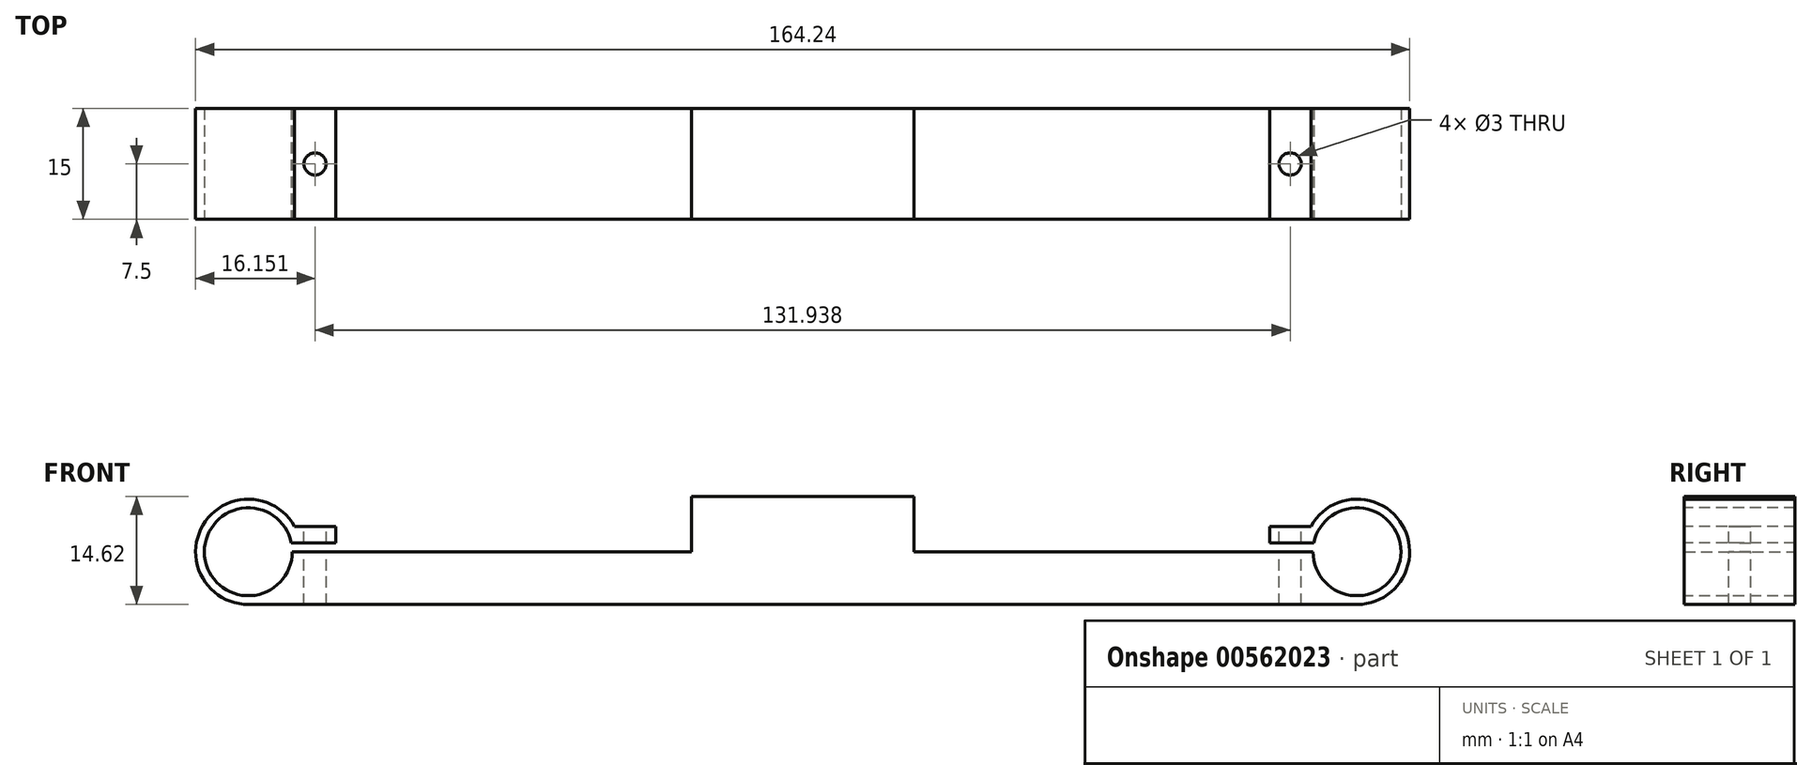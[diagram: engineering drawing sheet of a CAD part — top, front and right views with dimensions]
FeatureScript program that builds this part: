
annotation { "Feature Type Name" : "Feature", "Feature Type Description" : "" }
export const myFeature = defineFeature(function(context is Context, id is Id, definition is map)
    precondition{}
    {
        {
            var Q0;
            Q0=qCreatedBy(makeId("Front.planeOp"),FACE);
            var sketch = newSketch(context, id + "F0", { "sketchPlane" : qUnion([Q0])});
            skCircle(sketch, "E0", {"center": v(-75, 0) * mm, "radius": 5.95 * mm, "construction": true});
            skCircle(sketch, "E1", {"center": v(-75, 0) * mm, "radius": 7.12 * mm});
            skCircle(sketch, "E2", {"center": v(75, 0) * mm, "radius": 7.12 * mm});
            skLineSegment(sketch, "E3.bottom", {"start": v(-75, 0) * mm, "end": v(75.04, 0) * mm});
            skLineSegment(sketch, "E3.top", {"start": v(-75, -7.12) * mm, "end": v(75.04, -7.12) * mm});
            skLineSegment(sketch, "E3.left", {"start": v(-75, 0) * mm, "end": v(-75, -7.12) * mm});
            skLineSegment(sketch, "E3.right", {"start": v(75.04, 0) * mm, "end": v(75.04, -7.12) * mm});
            skSolve(sketch);
        }
        {
            var Q0;
            Q0=makeQuery(id+"F0.imprint","IMPRINT",FACE,{"disambiguationData":[TD([[makeQuery(id+"F0.imprint","IMPRINT",EDGE,{"derivedFrom":sQuery(id+"F0.wireOp",EDGE,"ZiFOfJtp-3PGB-lVWg-6YKo-kyjNysnR9mQS.bottom")}),-1.0]])]});
            var Q1;
            {var subQ0=sQuery(id+"F0.wireOp",EDGE,"ZiFOfJtp-3PGB-lVWg-6YKo-kyjNysnR9mQS.left");Q1=makeQuery(id+"F0.imprint","IMPRINT",FACE,{"disambiguationData":[TD([[makeQuery(id+"F0.imprint","IMPRINT",EDGE,{"derivedFrom":subQ0}),-1.0]])]});}
            var Q2;
            {var subQ0=sQuery(id+"F0.wireOp",EDGE,"ZiFOfJtp-3PGB-lVWg-6YKo-kyjNysnR9mQS.right");Q2=makeQuery(id+"F0.imprint","IMPRINT",FACE,{"disambiguationData":[TD([[makeQuery(id+"F0.imprint","IMPRINT",EDGE,{"derivedFrom":subQ0}),1.0]])]});}
            var Q3;
            {var subQ0=sQuery(id+"F0.wireOp",EDGE,"E3.top");Q3=makeQuery(id+"F0.imprint","IMPRINT",FACE,{"disambiguationData":[TD([[makeQuery(id+"F0.imprint","IMPRINT",EDGE,{"derivedFrom":subQ0}),1.0]])]});}
            var Q4;
            {var subQ0=sQuery(id+"F0.wireOp",EDGE,"E3.left");Q4=makeQuery(id+"F0.imprint","IMPRINT",FACE,{"disambiguationData":[TD([[makeQuery(id+"F0.imprint","IMPRINT",EDGE,{"derivedFrom":subQ0}),-1.0]])]});}
            var Q5;
            {var subQ0=sQuery(id+"F0.wireOp",EDGE,"E3.right");Q5=makeQuery(id+"F0.imprint","IMPRINT",FACE,{"disambiguationData":[TD([[makeQuery(id+"F0.imprint","IMPRINT",EDGE,{"derivedFrom":subQ0}),1.0]])]});}
            var Q6;
            {var subQ4=sQuery(id+"F0.wireOp",EDGE,"E3.right");Q6=makeQuery(id+"F0.imprint","IMPRINT",FACE,{"disambiguationData":[TD([[makeQuery(id+"F0.imprint","IMPRINT",EDGE,{"derivedFrom":subQ4}),-1.0]])]});}
            var Q7;
            {var subQ2=sQuery(id+"F0.wireOp",EDGE,"E3.left");Q7=makeQuery(id+"F0.imprint","IMPRINT",FACE,{"disambiguationData":[TD([[makeQuery(id+"F0.imprint","IMPRINT",EDGE,{"derivedFrom":subQ2}),1.0]])]});}
            extrude(context, id + "F1", {"entities" : qUnion([Q0, Q1, Q2, Q3, Q4, Q5, Q6, Q7]), "depth" : 15 * mm, "offsetDistance" : 25 * mm});
        }
        {
            var Q0;
            Q0=makeQuery(id+"F1.opExtrude","CAP_FACE",FACE,{"disambiguationData":[OSD([sQuery(id+"F0.wireOp",EDGE,"E1"),sQuery(id+"F0.wireOp",EDGE,"E2"),sQuery(id+"F0.wireOp",EDGE,"E3.bottom"),sQuery(id+"F0.wireOp",EDGE,"E3.top")])],"isStart":false});
            var sketch = newSketch(context, id + "F2", { "sketchPlane" : qUnion([Q0])});
            skCircle(sketch, "E4", {"center": v(-75, 0) * mm, "radius": 5.95 * mm});
            skCircle(sketch, "E5", {"center": v(75, 0) * mm, "radius": 5.95 * mm});
            skSolve(sketch);
        }
        {
            var Q0;
            Q0 = qSketchRegion(id + "F2", true);
            var Q1;
            Q1=sQuery(id+"F2.wireOp",EDGE,"E4");
            var Q2;
            Q2=sQuery(id+"F2.wireOp",EDGE,"E5");
            extrude(context, id + "F3", {"entities" : qUnion([Q0]), "operationType" : NewBodyOperationType.REMOVE, "surfaceEntities" : qUnion([Q1, Q2]), "endBound" : BoundingType.THROUGH_ALL, "oppositeDirection" : true, "depth" : 25 * mm, "offsetDistance" : 25 * mm});
        }
        {
            var Q0;
            Q0=makeQuery(id+"F1.opExtrude","CAP_FACE",FACE,{"disambiguationData":[OSD([sQuery(id+"F0.wireOp",EDGE,"E1"),sQuery(id+"F0.wireOp",EDGE,"E2"),sQuery(id+"F0.wireOp",EDGE,"E3.bottom"),sQuery(id+"F0.wireOp",EDGE,"E3.top")])],"isStart":false});
            var sketch = newSketch(context, id + "F4", { "sketchPlane" : qUnion([Q0])});
            skLineSegment(sketch, "E6.bottom", {"start": v(-75, 0) * mm, "end": v(75, 0) * mm});
            skLineSegment(sketch, "E6.top", {"start": v(-75, 1.2) * mm, "end": v(75, 1.2) * mm});
            skLineSegment(sketch, "E6.left", {"start": v(-75, 0) * mm, "end": v(-75, 1.2) * mm});
            skLineSegment(sketch, "E6.right", {"start": v(75, 0) * mm, "end": v(75, 1.2) * mm});
            skSolve(sketch);
        }
        {
            var Q0;
            {var subQ0=sQuery(id+"F4.wireOp",EDGE,"E6.bottom");var subQ1=makeQuery(id+"F1.opExtrude","CAP_EDGE",EDGE,{"disambiguationData":[OSD([sQuery(id+"F0.wireOp",EDGE,"E1")])],"isStart":false});var subQ2=makeQuery(id+"F4.imprint","INTERSECT",VERTEX,{"derivedFrom":[subQ1,subQ0]});Q0=makeQuery(id+"F4.imprint","IMPRINT",FACE,{"disambiguationData":[TD([[makeQuery(id+"F4.imprint","IMPRINT",EDGE,{"disambiguationData":[TD([[subQ2,-1.0]])],"derivedFrom":subQ0}),1.0]])]});}
            var Q1;
            {var subQ0=sQuery(id+"F4.wireOp",EDGE,"E6.bottom");var subQ1=makeQuery(id+"F1.opExtrude","CAP_EDGE",EDGE,{"disambiguationData":[OSD([sQuery(id+"F0.wireOp",EDGE,"E1")])],"isStart":false});var subQ2=makeQuery(id+"F4.imprint","INTERSECT",VERTEX,{"derivedFrom":[subQ1,subQ0]});Q1=makeQuery(id+"F4.imprint","IMPRINT",FACE,{"disambiguationData":[TD([[makeQuery(id+"F4.imprint","IMPRINT",EDGE,{"disambiguationData":[TD([[subQ2,1.0]])],"derivedFrom":subQ0}),1.0]])]});}
            var Q2;
            {var subQ0=sQuery(id+"F4.wireOp",EDGE,"E6.left");Q2=makeQuery(id+"F4.imprint","IMPRINT",FACE,{"disambiguationData":[TD([[makeQuery(id+"F4.imprint","IMPRINT",EDGE,{"derivedFrom":subQ0}),-1.0]])]});}
            var Q3;
            {var subQ0=sQuery(id+"F4.wireOp",EDGE,"E6.bottom");var subQ1=makeQuery(id+"F1.opExtrude","CAP_EDGE",EDGE,{"disambiguationData":[OSD([sQuery(id+"F0.wireOp",EDGE,"E2")])],"isStart":false});var subQ2=makeQuery(id+"F4.imprint","INTERSECT",VERTEX,{"derivedFrom":[subQ1,subQ0]});Q3=makeQuery(id+"F4.imprint","IMPRINT",FACE,{"disambiguationData":[TD([[makeQuery(id+"F4.imprint","IMPRINT",EDGE,{"disambiguationData":[TD([[subQ2,-1.0]])],"derivedFrom":subQ0}),1.0]])]});}
            var Q4;
            {var subQ0=sQuery(id+"F4.wireOp",EDGE,"E6.right");Q4=makeQuery(id+"F4.imprint","IMPRINT",FACE,{"disambiguationData":[TD([[makeQuery(id+"F4.imprint","IMPRINT",EDGE,{"derivedFrom":subQ0}),1.0]])]});}
            extrude(context, id + "F5", {"entities" : qUnion([Q0, Q1, Q2, Q3, Q4]), "operationType" : NewBodyOperationType.REMOVE, "oppositeDirection" : true, "depth" : 25 * mm, "offsetDistance" : 25 * mm});
        }
        {
            var Q0;
            Q0=makeQuery(id+"F1.opExtrude","CAP_FACE",FACE,{"disambiguationData":[OSD([sQuery(id+"F0.wireOp",EDGE,"E1"),sQuery(id+"F0.wireOp",EDGE,"E2"),sQuery(id+"F0.wireOp",EDGE,"E3.bottom"),sQuery(id+"F0.wireOp",EDGE,"E3.top")])],"isStart":false});
            var sketch = newSketch(context, id + "F6", { "sketchPlane" : qUnion([Q0])});
            skLineSegment(sketch, "E7.bottom", {"start": v(-69.17, 1.2) * mm, "end": v(-63.17, 1.2) * mm});
            skLineSegment(sketch, "E7.top", {"start": v(-69.17, 3.45) * mm, "end": v(-63.17, 3.45) * mm});
            skLineSegment(sketch, "E7.left", {"start": v(-69.17, 1.2) * mm, "end": v(-69.17, 3.45) * mm});
            skLineSegment(sketch, "E7.right", {"start": v(-63.17, 1.2) * mm, "end": v(-63.17, 3.45) * mm});
            skLineSegment(sketch, "E8.bottom", {"start": v(69.17, 1.2) * mm, "end": v(63.17, 1.2) * mm});
            skLineSegment(sketch, "E8.top", {"start": v(69.17, 3.45) * mm, "end": v(63.17, 3.45) * mm});
            skLineSegment(sketch, "E8.left", {"start": v(69.17, 1.2) * mm, "end": v(69.17, 3.45) * mm});
            skLineSegment(sketch, "E8.right", {"start": v(63.17, 1.2) * mm, "end": v(63.17, 3.45) * mm});
            skSolve(sketch);
        }
        {
            var Q0;
            {var subQ3=sQuery(id+"F6.wireOp",EDGE,"E7.right");Q0=makeQuery(id+"F6.imprint","IMPRINT",FACE,{"disambiguationData":[TD([[makeQuery(id+"F6.imprint","IMPRINT",EDGE,{"derivedFrom":subQ3}),1.0]])]});}
            var Q1;
            {var subQ3=sQuery(id+"F6.wireOp",EDGE,"E8.right");Q1=makeQuery(id+"F6.imprint","IMPRINT",FACE,{"disambiguationData":[TD([[makeQuery(id+"F6.imprint","IMPRINT",EDGE,{"derivedFrom":subQ3}),-1.0]])]});}
            extrude(context, id + "F7", {"entities" : qUnion([Q0, Q1]), "operationType" : NewBodyOperationType.ADD, "oppositeDirection" : true, "depth" : 15 * mm, "offsetDistance" : 25 * mm});
        }
        {
            var Q0;
            Q0=makeQuery(id+"F7.opExtrude","SWEPT_FACE",FACE,{"disambiguationData":[OSD([sQuery(id+"F6.wireOp",EDGE,"E7.top")])]});
            var sketch = newSketch(context, id + "F8", { "sketchPlane" : qUnion([Q0])});
            skPoint(sketch, "E9", {"position": v(-65.97, 0) * mm});
            skPoint(sketch, "E10", {"position": v(-68.77, -7.5) * mm});
            skLineSegment(sketch, "E11", {"start": v(-65.97, 0) * mm, "end": v(-65.97, -15) * mm, "construction": true});
            skCircle(sketch, "E12", {"center": v(-65.97, -7.5) * mm, "radius": 1.5 * mm});
            skCircle(sketch, "E13", {"center": v(65.97, -7.5) * mm, "radius": 1.5 * mm});
            skSolve(sketch);
        }
        {
            var Q0;
            Q0=makeQuery(id+"F8.imprint","IMPRINT",FACE,{"disambiguationData":[TD([[makeQuery(id+"F8.imprint","IMPRINT",EDGE,{"derivedFrom":sQuery(id+"F8.wireOp",EDGE,"E12")}),1.0]])]});
            var Q1;
            Q1=makeQuery(id+"F8.imprint","IMPRINT",FACE,{"disambiguationData":[TD([[makeQuery(id+"F8.imprint","IMPRINT",EDGE,{"derivedFrom":sQuery(id+"F8.wireOp",EDGE,"E13")}),1.0]])]});
            var Q2;
            Q2=sQuery(id+"F8.wireOp",EDGE,"E12");
            extrude(context, id + "F9", {"entities" : qUnion([Q0, Q1]), "operationType" : NewBodyOperationType.REMOVE, "surfaceEntities" : qUnion([Q2]), "oppositeDirection" : true, "depth" : 25 * mm, "offsetDistance" : 25 * mm});
        }
        {
            var Q0;
            Q0=makeQuery(id+"F5.boolean.opBoolean","MERGE",FACE,{"derivedFrom":[makeQuery(id+"F1.opExtrude","SWEPT_FACE",FACE,{"disambiguationData":[OSD([sQuery(id+"F0.wireOp",EDGE,"E3.bottom")])]}),makeQuery(id+"F5.opExtrude","SWEPT_FACE",FACE,{"disambiguationData":[OSD([sQuery(id+"F4.wireOp",EDGE,"E6.bottom")])]})]});
            var sketch = newSketch(context, id + "F10", { "sketchPlane" : qUnion([Q0])});
            skLineSegment(sketch, "E14", {"start": v(0, -15) * mm, "end": v(0, 0) * mm, "construction": true});
            skLineSegment(sketch, "E15.bottom", {"start": v(-15.06, -15) * mm, "end": v(15.06, -15) * mm});
            skLineSegment(sketch, "E15.top", {"start": v(-15.06, 0) * mm, "end": v(15.06, 0) * mm});
            skLineSegment(sketch, "E15.left", {"start": v(-15.06, -15) * mm, "end": v(-15.06, 0) * mm});
            skLineSegment(sketch, "E15.right", {"start": v(15.06, -15) * mm, "end": v(15.06, 0) * mm});
            skPoint(sketch, "E15.middle", {"position": v(0, -7.5) * mm});
            skSolve(sketch);
        }
        {
            var Q0;
            Q0 = qSketchRegion(id + "F10", true);
            extrude(context, id + "F11", {"entities" : qUnion([Q0]), "operationType" : NewBodyOperationType.ADD, "depth" : 7.5 * mm, "offsetDistance" : 25 * mm});
        }
    });
